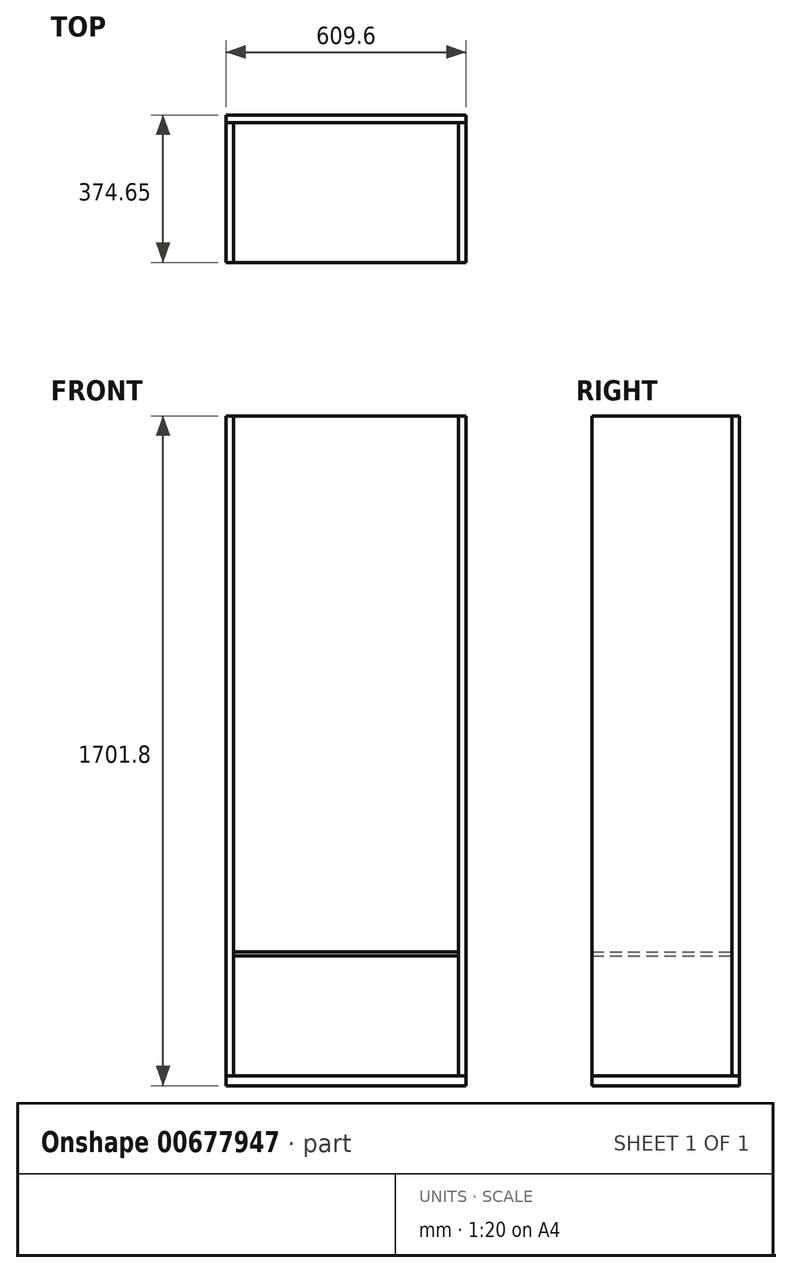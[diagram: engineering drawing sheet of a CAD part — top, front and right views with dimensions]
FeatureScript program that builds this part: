
annotation { "Feature Type Name" : "Feature", "Feature Type Description" : "" }
export const myFeature = defineFeature(function(context is Context, id is Id, definition is map)
    precondition{}
    {
        {
            var Q0;
            Q0=qCreatedBy(makeId("Top.planeOp"),FACE);
            var sketch = newSketch(context, id + "F0", { "sketchPlane" : qUnion([Q0])});
            skLineSegment(sketch, "E0.bottom", {"start": v(304.8, 177.8) * mm, "end": v(-304.8, 177.8) * mm});
            skLineSegment(sketch, "E0.top", {"start": v(304.8, -177.8) * mm, "end": v(-304.8, -177.8) * mm});
            skLineSegment(sketch, "E0.left", {"start": v(304.8, 177.8) * mm, "end": v(304.8, -177.8) * mm});
            skLineSegment(sketch, "E0.right", {"start": v(-304.8, 177.8) * mm, "end": v(-304.8, -177.8) * mm});
            skPoint(sketch, "E0.middle", {"position": v(0, 0) * mm});
            skLineSegment(sketch, "E1.0", {"start": v(-285.75, 177.8) * mm, "end": v(-285.75, -177.8) * mm});
            skLineSegment(sketch, "E2.0", {"start": v(285.75, 177.8) * mm, "end": v(285.75, -177.8) * mm});
            skLineSegment(sketch, "E3.0", {"start": v(304.8, 196.85) * mm, "end": v(-304.8, 196.85) * mm});
            skLineSegment(sketch, "E4", {"start": v(-304.8, 196.85) * mm, "end": v(-304.8, 177.8) * mm});
            skLineSegment(sketch, "E5", {"start": v(304.8, 196.85) * mm, "end": v(304.8, 177.8) * mm});
            skSolve(sketch);
        }
        {
            var Q0;
            Q0=makeQuery(id+"F0.imprint","IMPRINT",FACE,{"disambiguationData":[TD([[makeQuery(id+"F0.imprint","IMPRINT",EDGE,{"derivedFrom":sQuery(id+"F0.wireOp",EDGE,"E3.0")}),1.0]])]});
            extrude(context, id + "F1", {"entities" : qUnion([Q0]), "depth" : 1676.4 * mm, "offsetDistance" : 25.4 * mm});
        }
        {
            var Q0;
            {var subQ0=sQuery(id+"F0.wireOp",EDGE,"E0.right");Q0=makeQuery(id+"F0.imprint","IMPRINT",FACE,{"disambiguationData":[TD([[makeQuery(id+"F0.imprint","IMPRINT",EDGE,{"derivedFrom":subQ0}),1.0]])]});}
            var Q1;
            {var subQ0=sQuery(id+"F0.wireOp",EDGE,"E0.left");Q1=makeQuery(id+"F0.imprint","IMPRINT",FACE,{"disambiguationData":[TD([[makeQuery(id+"F0.imprint","IMPRINT",EDGE,{"derivedFrom":subQ0}),-1.0]])]});}
            extrude(context, id + "F2", {"entities" : qUnion([Q0, Q1]), "depth" : 1676.4 * mm, "offsetDistance" : 25.4 * mm});
        }
        {
            var Q0;
            Q0 = qSketchRegion(id + "F0", true);
            extrude(context, id + "F3", {"entities" : qUnion([Q0]), "oppositeDirection" : true, "depth" : 25.4 * mm, "offsetDistance" : 25.4 * mm});
        }
        {
            var Q0;
            Q0=makeQuery(id+"F1.opExtrude","SWEPT_FACE",FACE,{"disambiguationData":[OSD([sQuery(id+"F0.wireOp",EDGE,"E0.bottom")])]});
            var sketch = newSketch(context, id + "F4", { "sketchPlane" : qUnion([Q0])});
            skLineSegment(sketch, "E6.0", {"start": v(-285.75, 1676.4) * mm, "end": v(-285.75, 0) * mm});
            skLineSegment(sketch, "E7.0", {"start": v(285.75, 1676.4) * mm, "end": v(285.75, 0) * mm});
            skLineSegment(sketch, "E8.bottom", {"start": v(-285.75, 304.8) * mm, "end": v(285.75, 304.8) * mm});
            skLineSegment(sketch, "E8.top", {"start": v(-285.75, 314.33) * mm, "end": v(285.75, 314.33) * mm});
            skLineSegment(sketch, "E8.left", {"start": v(-285.75, 304.8) * mm, "end": v(-285.75, 314.33) * mm});
            skLineSegment(sketch, "E8.right", {"start": v(285.75, 304.8) * mm, "end": v(285.75, 314.32) * mm});
            skSolve(sketch);
        }
        {
            var Q0;
            Q0=makeQuery(id+"F4.imprint","IMPRINT",FACE,{"disambiguationData":[TD([[makeQuery(id+"F4.imprint","IMPRINT",EDGE,{"derivedFrom":sQuery(id+"F4.wireOp",EDGE,"E8.bottom")}),1.0]])]});
            var Q1;
            {var subQ0=sQuery(id+"F0.wireOp",EDGE,"E0.top");Q1=makeQuery(id+"F2.opExtrude","SWEPT_FACE",FACE,{"disambiguationData":[OSD([subQ0]),TDD([makeQuery(id+"F0.imprint","IMPRINT",EDGE,{"disambiguationData":[TD([[makeQuery(id+"F0.imprint","INTERSECT",VERTEX,{"derivedFrom":[subQ0,sQuery(id+"F0.wireOp",EDGE,"E0.right")]}),1.0]])],"derivedFrom":subQ0})])]});}
            extrude(context, id + "F5", {"entities" : qUnion([Q0]), "endBound" : BoundingType.UP_TO_SURFACE, "depth" : 25.4 * mm, "endBoundEntityFace" : qUnion([Q1]), "offsetDistance" : 25.4 * mm});
        }
    });
